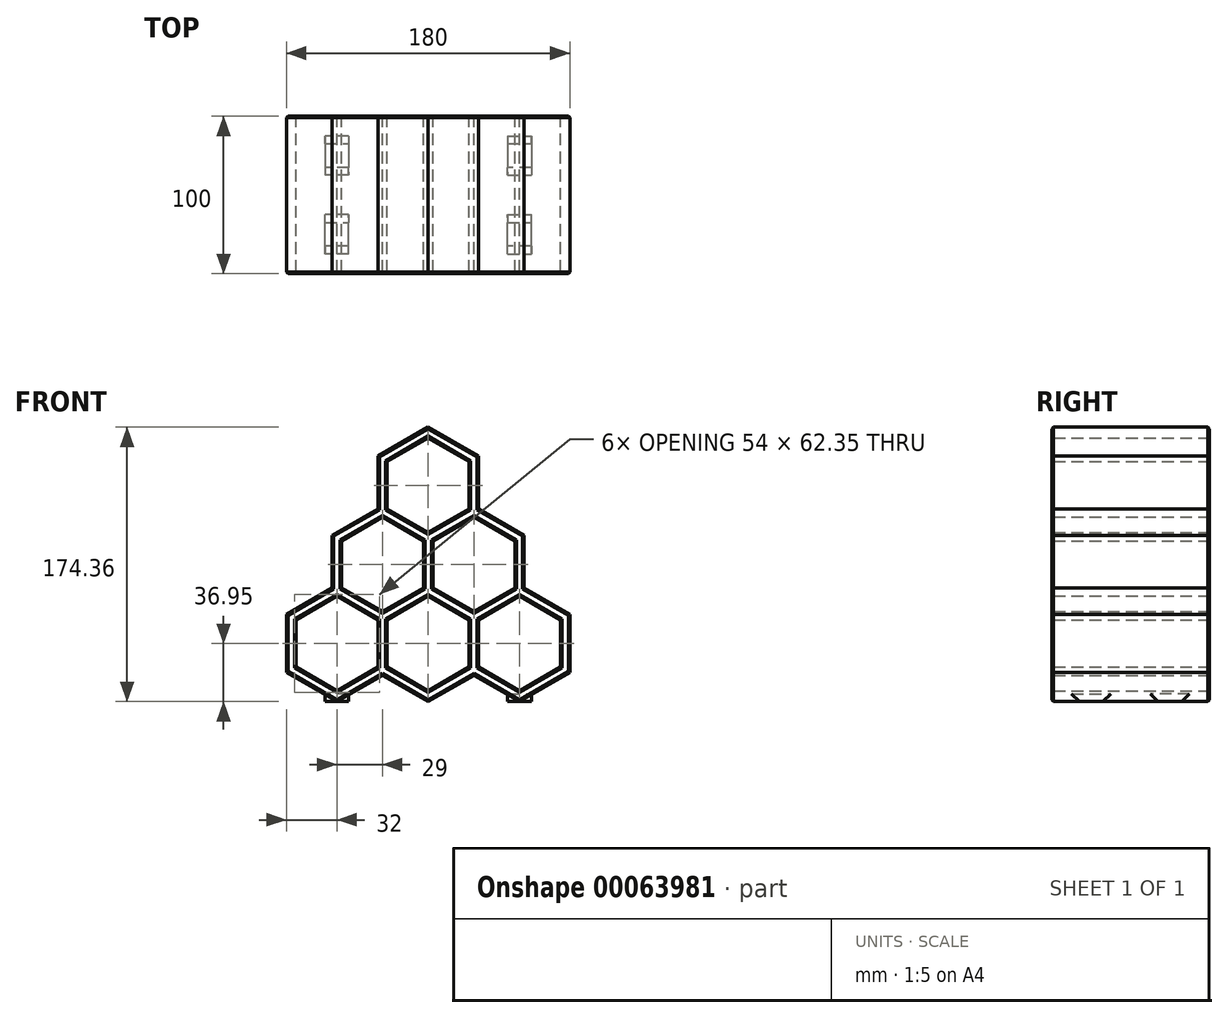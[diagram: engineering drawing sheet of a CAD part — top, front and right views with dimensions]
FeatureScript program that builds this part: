
annotation { "Feature Type Name" : "Feature", "Feature Type Description" : "" }
export const myFeature = defineFeature(function(context is Context, id is Id, definition is map)
    precondition{}
    {
        {
            var Q0;
            Q0=qCreatedBy(makeId("Front.planeOp"),FACE);
            var sketch = newSketch(context, id + "F0", { "sketchPlane" : qUnion([Q0])});
            skCircle(sketch, "E0.cCircle", {"center": v(0, 0) * mm, "radius": 32 * mm, "construction": true});
            skLineSegment(sketch, "E0.0", {"start": v(32, 18.48) * mm, "end": v(32, -18.48) * mm});
            skLineSegment(sketch, "E0.1", {"start": v(32, -18.48) * mm, "end": v(0, -36.95) * mm});
            skLineSegment(sketch, "E0.2", {"start": v(0, -36.95) * mm, "end": v(-32, -18.48) * mm});
            skLineSegment(sketch, "E0.3", {"start": v(-32, -18.48) * mm, "end": v(-32, 18.48) * mm});
            skLineSegment(sketch, "E0.4", {"start": v(-32, 18.48) * mm, "end": v(0, 36.95) * mm});
            skLineSegment(sketch, "E0.5", {"start": v(0, 36.95) * mm, "end": v(32, 18.48) * mm});
            skPoint(sketch, "E0.0.midPoint", {"position": v(32, 0) * mm});
            skCircle(sketch, "E1.cCircle", {"center": v(0, 0) * mm, "radius": 26 * mm, "construction": true});
            skLineSegment(sketch, "E1.0", {"start": v(26, 15.01) * mm, "end": v(26, -15.01) * mm});
            skLineSegment(sketch, "E1.1", {"start": v(26, -15.01) * mm, "end": v(0, -30.02) * mm});
            skLineSegment(sketch, "E1.2", {"start": v(0, -30.02) * mm, "end": v(-26, -15.01) * mm});
            skLineSegment(sketch, "E1.3", {"start": v(-26, -15.01) * mm, "end": v(-26, 15.01) * mm});
            skLineSegment(sketch, "E1.4", {"start": v(-26, 15.01) * mm, "end": v(0, 30.02) * mm});
            skLineSegment(sketch, "E1.5", {"start": v(0, 30.02) * mm, "end": v(26, 15.01) * mm});
            skPoint(sketch, "E1.0.midPoint", {"position": v(26, 0) * mm});
            skSolve(sketch);
        }
        {
            var Q0;
            Q0 = qSketchRegion(id + "F0", true);
            extrude(context, id + "F1", {"entities" : qUnion([Q0]), "depth" : 100 * mm});
        }
        {
            var Q0;
            Q0=makeQuery(id+"F1.opExtrude","CAP_EDGE",EDGE,{"disambiguationData":[OSD([sQuery(id+"F0.wireOp",EDGE,"E1.3")])],"isStart":false});
            cPoint(context, id + "F2", {"entities" : qUnion([Q0]), "parameter" : 0.5});
        }
        {
            var Q0;
            Q0=makeQuery(id+"F1.opExtrude","CAP_EDGE",EDGE,{"disambiguationData":[OSD([sQuery(id+"F0.wireOp",EDGE,"E0.0")])],"isStart":false});
            cPoint(context, id + "F3", {"entities" : qUnion([Q0]), "parameter" : 0.5});
        }
        {
            var Q0;
            Q0=makeQuery(id+"F1.opExtrude","SWEPT_BODY",BODY,{"disambiguationData":[OSD([sQuery(id+"F0.wireOp",EDGE,"E0.0"),sQuery(id+"F0.wireOp",EDGE,"E0.1"),sQuery(id+"F0.wireOp",EDGE,"E0.2"),sQuery(id+"F0.wireOp",EDGE,"E0.3"),sQuery(id+"F0.wireOp",EDGE,"E0.4"),sQuery(id+"F0.wireOp",EDGE,"E0.5"),sQuery(id+"F0.wireOp",EDGE,"E1.0"),sQuery(id+"F0.wireOp",EDGE,"E1.1"),sQuery(id+"F0.wireOp",EDGE,"E1.2"),sQuery(id+"F0.wireOp",EDGE,"E1.3"),sQuery(id+"F0.wireOp",EDGE,"E1.4"),sQuery(id+"F0.wireOp",EDGE,"E1.5")])]});
            var Q1;
            Q1 = qCreatedBy(id + "F2" ,VERTEX);
            var Q2;
            Q2 = qCreatedBy(id + "F3" ,VERTEX);
            transform(context, id + "F4", {"entities" : qUnion([Q0]), "transformType" : TransformType.TRANSLATION_ENTITY, "oppositeDirectionEntity" : false, "transformLine" : qUnion([Q1, Q2]), "makeCopy" : true});
        }
        {
            var Q0;
            Q0=makeQuery(id+"F1.opExtrude","CAP_EDGE",EDGE,{"disambiguationData":[OSD([sQuery(id+"F0.wireOp",EDGE,"E1.3")])],"isStart":false});
            cPoint(context, id + "F5", {"entities" : qUnion([Q0]), "parameter" : 0.5});
        }
        {
            var Q0;
            Q0=makeQuery(id+"F4.opPattern","COPY",EDGE,{"derivedFrom":makeQuery(id+"F1.opExtrude","CAP_EDGE",EDGE,{"disambiguationData":[OSD([sQuery(id+"F0.wireOp",EDGE,"E0.0")])],"isStart":false}),"instanceName":"1"});
            cPoint(context, id + "F6", {"entities" : qUnion([Q0]), "parameter" : 0.5});
        }
        {
            var Q0;
            Q0=makeQuery(id+"F1.opExtrude","SWEPT_BODY",BODY,{"disambiguationData":[OSD([sQuery(id+"F0.wireOp",EDGE,"E0.0"),sQuery(id+"F0.wireOp",EDGE,"E0.1"),sQuery(id+"F0.wireOp",EDGE,"E0.2"),sQuery(id+"F0.wireOp",EDGE,"E0.3"),sQuery(id+"F0.wireOp",EDGE,"E0.4"),sQuery(id+"F0.wireOp",EDGE,"E0.5"),sQuery(id+"F0.wireOp",EDGE,"E1.0"),sQuery(id+"F0.wireOp",EDGE,"E1.1"),sQuery(id+"F0.wireOp",EDGE,"E1.2"),sQuery(id+"F0.wireOp",EDGE,"E1.3"),sQuery(id+"F0.wireOp",EDGE,"E1.4"),sQuery(id+"F0.wireOp",EDGE,"E1.5")])]});
            var Q1;
            Q1 = qCreatedBy(id + "F5" ,VERTEX);
            var Q2;
            Q2 = qCreatedBy(id + "F6" ,VERTEX);
            transform(context, id + "F7", {"entities" : qUnion([Q0]), "transformType" : TransformType.TRANSLATION_ENTITY, "oppositeDirectionEntity" : false, "transformLine" : qUnion([Q1, Q2]), "makeCopy" : true});
        }
        {
            var Q0;
            Q0=makeQuery(id+"F1.opExtrude","CAP_EDGE",EDGE,{"disambiguationData":[OSD([sQuery(id+"F0.wireOp",EDGE,"E0.2")])],"isStart":false});
            cPoint(context, id + "F8", {"entities" : qUnion([Q0]), "parameter" : 0.5});
        }
        {
            var Q0;
            Q0=makeQuery(id+"F1.opExtrude","CAP_EDGE",EDGE,{"disambiguationData":[OSD([sQuery(id+"F0.wireOp",EDGE,"E1.5")])],"isStart":false});
            cPoint(context, id + "F9", {"entities" : qUnion([Q0]), "parameter" : 0.5});
        }
        {
            var Q0;
            Q0=makeQuery(id+"F1.opExtrude","SWEPT_BODY",BODY,{"disambiguationData":[OSD([sQuery(id+"F0.wireOp",EDGE,"E0.0"),sQuery(id+"F0.wireOp",EDGE,"E0.1"),sQuery(id+"F0.wireOp",EDGE,"E0.2"),sQuery(id+"F0.wireOp",EDGE,"E0.3"),sQuery(id+"F0.wireOp",EDGE,"E0.4"),sQuery(id+"F0.wireOp",EDGE,"E0.5"),sQuery(id+"F0.wireOp",EDGE,"E1.0"),sQuery(id+"F0.wireOp",EDGE,"E1.1"),sQuery(id+"F0.wireOp",EDGE,"E1.2"),sQuery(id+"F0.wireOp",EDGE,"E1.3"),sQuery(id+"F0.wireOp",EDGE,"E1.4"),sQuery(id+"F0.wireOp",EDGE,"E1.5")])]});
            var Q1;
            Q1 = qCreatedBy(id + "F8" ,VERTEX);
            var Q2;
            Q2 = qCreatedBy(id + "F9" ,VERTEX);
            transform(context, id + "F10", {"entities" : qUnion([Q0]), "transformType" : TransformType.TRANSLATION_ENTITY, "oppositeDirectionEntity" : false, "transformLine" : qUnion([Q1, Q2]), "makeCopy" : true});
        }
        {
            var Q0;
            Q0=makeQuery(id+"F1.opExtrude","CAP_EDGE",EDGE,{"disambiguationData":[OSD([sQuery(id+"F0.wireOp",EDGE,"E0.2")])],"isStart":false});
            cPoint(context, id + "F11", {"entities" : qUnion([Q0]), "parameter" : 0.5});
        }
        {
            var Q0;
            Q0=makeQuery(id+"F4.opPattern","COPY",EDGE,{"derivedFrom":makeQuery(id+"F1.opExtrude","CAP_EDGE",EDGE,{"disambiguationData":[OSD([sQuery(id+"F0.wireOp",EDGE,"E1.5")])],"isStart":false}),"instanceName":"1"});
            cPoint(context, id + "F12", {"entities" : qUnion([Q0]), "parameter" : 0.5});
        }
        {
            var Q0;
            Q0=makeQuery(id+"F1.opExtrude","SWEPT_BODY",BODY,{"disambiguationData":[OSD([sQuery(id+"F0.wireOp",EDGE,"E0.0"),sQuery(id+"F0.wireOp",EDGE,"E0.1"),sQuery(id+"F0.wireOp",EDGE,"E0.2"),sQuery(id+"F0.wireOp",EDGE,"E0.3"),sQuery(id+"F0.wireOp",EDGE,"E0.4"),sQuery(id+"F0.wireOp",EDGE,"E0.5"),sQuery(id+"F0.wireOp",EDGE,"E1.0"),sQuery(id+"F0.wireOp",EDGE,"E1.1"),sQuery(id+"F0.wireOp",EDGE,"E1.2"),sQuery(id+"F0.wireOp",EDGE,"E1.3"),sQuery(id+"F0.wireOp",EDGE,"E1.4"),sQuery(id+"F0.wireOp",EDGE,"E1.5")])]});
            var Q1;
            Q1 = qCreatedBy(id + "F11" ,VERTEX);
            var Q2;
            Q2 = qCreatedBy(id + "F12" ,VERTEX);
            transform(context, id + "F13", {"entities" : qUnion([Q0]), "transformType" : TransformType.TRANSLATION_ENTITY, "oppositeDirectionEntity" : false, "transformLine" : qUnion([Q1, Q2]), "makeCopy" : true});
        }
        {
            var Q0;
            Q0=makeQuery(id+"F1.opExtrude","CAP_EDGE",EDGE,{"disambiguationData":[OSD([sQuery(id+"F0.wireOp",EDGE,"E0.2")])],"isStart":false});
            cPoint(context, id + "F14", {"entities" : qUnion([Q0]), "parameter" : 0.5});
        }
        {
            var Q0;
            Q0=makeQuery(id+"F10.opPattern","COPY",EDGE,{"derivedFrom":makeQuery(id+"F1.opExtrude","CAP_EDGE",EDGE,{"disambiguationData":[OSD([sQuery(id+"F0.wireOp",EDGE,"E1.5")])],"isStart":false}),"instanceName":"1"});
            cPoint(context, id + "F15", {"entities" : qUnion([Q0]), "parameter" : 0.5});
        }
        {
            var Q0;
            Q0=makeQuery(id+"F1.opExtrude","SWEPT_BODY",BODY,{"disambiguationData":[OSD([sQuery(id+"F0.wireOp",EDGE,"E0.0"),sQuery(id+"F0.wireOp",EDGE,"E0.1"),sQuery(id+"F0.wireOp",EDGE,"E0.2"),sQuery(id+"F0.wireOp",EDGE,"E0.3"),sQuery(id+"F0.wireOp",EDGE,"E0.4"),sQuery(id+"F0.wireOp",EDGE,"E0.5"),sQuery(id+"F0.wireOp",EDGE,"E1.0"),sQuery(id+"F0.wireOp",EDGE,"E1.1"),sQuery(id+"F0.wireOp",EDGE,"E1.2"),sQuery(id+"F0.wireOp",EDGE,"E1.3"),sQuery(id+"F0.wireOp",EDGE,"E1.4"),sQuery(id+"F0.wireOp",EDGE,"E1.5")])]});
            var Q1;
            Q1 = qCreatedBy(id + "F14" ,VERTEX);
            var Q2;
            Q2 = qCreatedBy(id + "F15" ,VERTEX);
            transform(context, id + "F16", {"entities" : qUnion([Q0]), "transformType" : TransformType.TRANSLATION_ENTITY, "oppositeDirectionEntity" : false, "transformLine" : qUnion([Q1, Q2]), "makeCopy" : true});
        }
        {
            var Q0;
            Q0=makeQuery(id+"F1.opExtrude","SWEPT_BODY",BODY,{"disambiguationData":[OSD([sQuery(id+"F0.wireOp",EDGE,"E0.0"),sQuery(id+"F0.wireOp",EDGE,"E0.1"),sQuery(id+"F0.wireOp",EDGE,"E0.2"),sQuery(id+"F0.wireOp",EDGE,"E0.3"),sQuery(id+"F0.wireOp",EDGE,"E0.4"),sQuery(id+"F0.wireOp",EDGE,"E0.5"),sQuery(id+"F0.wireOp",EDGE,"E1.0"),sQuery(id+"F0.wireOp",EDGE,"E1.1"),sQuery(id+"F0.wireOp",EDGE,"E1.2"),sQuery(id+"F0.wireOp",EDGE,"E1.3"),sQuery(id+"F0.wireOp",EDGE,"E1.4"),sQuery(id+"F0.wireOp",EDGE,"E1.5")])]});
            var Q1;
            Q1=makeQuery(id+"F10.opPattern","COPY",BODY,{"derivedFrom":makeQuery(id+"F1.opExtrude","SWEPT_BODY",BODY,{"disambiguationData":[OSD([sQuery(id+"F0.wireOp",EDGE,"E0.0"),sQuery(id+"F0.wireOp",EDGE,"E0.1"),sQuery(id+"F0.wireOp",EDGE,"E0.2"),sQuery(id+"F0.wireOp",EDGE,"E0.3"),sQuery(id+"F0.wireOp",EDGE,"E0.4"),sQuery(id+"F0.wireOp",EDGE,"E0.5"),sQuery(id+"F0.wireOp",EDGE,"E1.0"),sQuery(id+"F0.wireOp",EDGE,"E1.1"),sQuery(id+"F0.wireOp",EDGE,"E1.2"),sQuery(id+"F0.wireOp",EDGE,"E1.3"),sQuery(id+"F0.wireOp",EDGE,"E1.4"),sQuery(id+"F0.wireOp",EDGE,"E1.5")])]}),"instanceName":"1"});
            var Q2;
            Q2=makeQuery(id+"F16.opPattern","COPY",BODY,{"derivedFrom":makeQuery(id+"F1.opExtrude","SWEPT_BODY",BODY,{"disambiguationData":[OSD([sQuery(id+"F0.wireOp",EDGE,"E0.0"),sQuery(id+"F0.wireOp",EDGE,"E0.1"),sQuery(id+"F0.wireOp",EDGE,"E0.2"),sQuery(id+"F0.wireOp",EDGE,"E0.3"),sQuery(id+"F0.wireOp",EDGE,"E0.4"),sQuery(id+"F0.wireOp",EDGE,"E0.5"),sQuery(id+"F0.wireOp",EDGE,"E1.0"),sQuery(id+"F0.wireOp",EDGE,"E1.1"),sQuery(id+"F0.wireOp",EDGE,"E1.2"),sQuery(id+"F0.wireOp",EDGE,"E1.3"),sQuery(id+"F0.wireOp",EDGE,"E1.4"),sQuery(id+"F0.wireOp",EDGE,"E1.5")])]}),"instanceName":"1"});
            var Q3;
            Q3=makeQuery(id+"F4.opPattern","COPY",BODY,{"derivedFrom":makeQuery(id+"F1.opExtrude","SWEPT_BODY",BODY,{"disambiguationData":[OSD([sQuery(id+"F0.wireOp",EDGE,"E0.0"),sQuery(id+"F0.wireOp",EDGE,"E0.1"),sQuery(id+"F0.wireOp",EDGE,"E0.2"),sQuery(id+"F0.wireOp",EDGE,"E0.3"),sQuery(id+"F0.wireOp",EDGE,"E0.4"),sQuery(id+"F0.wireOp",EDGE,"E0.5"),sQuery(id+"F0.wireOp",EDGE,"E1.0"),sQuery(id+"F0.wireOp",EDGE,"E1.1"),sQuery(id+"F0.wireOp",EDGE,"E1.2"),sQuery(id+"F0.wireOp",EDGE,"E1.3"),sQuery(id+"F0.wireOp",EDGE,"E1.4"),sQuery(id+"F0.wireOp",EDGE,"E1.5")])]}),"instanceName":"1"});
            var Q4;
            Q4=makeQuery(id+"F13.opPattern","COPY",BODY,{"derivedFrom":makeQuery(id+"F1.opExtrude","SWEPT_BODY",BODY,{"disambiguationData":[OSD([sQuery(id+"F0.wireOp",EDGE,"E0.0"),sQuery(id+"F0.wireOp",EDGE,"E0.1"),sQuery(id+"F0.wireOp",EDGE,"E0.2"),sQuery(id+"F0.wireOp",EDGE,"E0.3"),sQuery(id+"F0.wireOp",EDGE,"E0.4"),sQuery(id+"F0.wireOp",EDGE,"E0.5"),sQuery(id+"F0.wireOp",EDGE,"E1.0"),sQuery(id+"F0.wireOp",EDGE,"E1.1"),sQuery(id+"F0.wireOp",EDGE,"E1.2"),sQuery(id+"F0.wireOp",EDGE,"E1.3"),sQuery(id+"F0.wireOp",EDGE,"E1.4"),sQuery(id+"F0.wireOp",EDGE,"E1.5")])]}),"instanceName":"1"});
            var Q5;
            Q5=makeQuery(id+"F7.opPattern","COPY",BODY,{"derivedFrom":makeQuery(id+"F1.opExtrude","SWEPT_BODY",BODY,{"disambiguationData":[OSD([sQuery(id+"F0.wireOp",EDGE,"E0.0"),sQuery(id+"F0.wireOp",EDGE,"E0.1"),sQuery(id+"F0.wireOp",EDGE,"E0.2"),sQuery(id+"F0.wireOp",EDGE,"E0.3"),sQuery(id+"F0.wireOp",EDGE,"E0.4"),sQuery(id+"F0.wireOp",EDGE,"E0.5"),sQuery(id+"F0.wireOp",EDGE,"E1.0"),sQuery(id+"F0.wireOp",EDGE,"E1.1"),sQuery(id+"F0.wireOp",EDGE,"E1.2"),sQuery(id+"F0.wireOp",EDGE,"E1.3"),sQuery(id+"F0.wireOp",EDGE,"E1.4"),sQuery(id+"F0.wireOp",EDGE,"E1.5")])]}),"instanceName":"1"});
            booleanBodies(context, id + "F17", {"operationType" : BooleanOperationType.UNION, "tools" : qUnion([Q0, Q1, Q2, Q3, Q4, Q5])});
        }
        {
            var Q0;
            Q0=makeQuery(id+"F4.opPattern","COPY",EDGE,{"derivedFrom":makeQuery(id+"F1.opExtrude","CAP_EDGE",EDGE,{"disambiguationData":[OSD([sQuery(id+"F0.wireOp",EDGE,"E1.0")])],"isStart":false}),"instanceName":"1"});
            cPoint(context, id + "F18", {"entities" : qUnion([Q0]), "parameter" : 0.5});
        }
        {
            var Q0;
            Q0=makeQuery(id+"F1.opExtrude","CAP_EDGE",EDGE,{"disambiguationData":[OSD([sQuery(id+"F0.wireOp",EDGE,"E1.0")])],"isStart":false});
            cPoint(context, id + "F19", {"entities" : qUnion([Q0]), "parameter" : 0.5});
        }
        {
            var Q0;
            Q0=makeQuery(id+"F1.opExtrude","SWEPT_BODY",BODY,{"disambiguationData":[OSD([sQuery(id+"F0.wireOp",EDGE,"E0.0"),sQuery(id+"F0.wireOp",EDGE,"E0.1"),sQuery(id+"F0.wireOp",EDGE,"E0.2"),sQuery(id+"F0.wireOp",EDGE,"E0.3"),sQuery(id+"F0.wireOp",EDGE,"E0.4"),sQuery(id+"F0.wireOp",EDGE,"E0.5"),sQuery(id+"F0.wireOp",EDGE,"E1.0"),sQuery(id+"F0.wireOp",EDGE,"E1.1"),sQuery(id+"F0.wireOp",EDGE,"E1.2"),sQuery(id+"F0.wireOp",EDGE,"E1.3"),sQuery(id+"F0.wireOp",EDGE,"E1.4"),sQuery(id+"F0.wireOp",EDGE,"E1.5")])]});
            var Q1;
            Q1 = qCreatedBy(id + "F18" ,VERTEX);
            var Q2;
            Q2 = qCreatedBy(id + "F19" ,VERTEX);
            transform(context, id + "F20", {"entities" : qUnion([Q0]), "transformType" : TransformType.TRANSLATION_ENTITY, "oppositeDirectionEntity" : false, "transformLine" : qUnion([Q1, Q2]), "makeCopy" : false});
        }
        {
            var Q0;
            Q0=makeQuery(id+"F1.opExtrude","SWEPT_BODY",BODY,{"disambiguationData":[OSD([sQuery(id+"F0.wireOp",EDGE,"E0.0"),sQuery(id+"F0.wireOp",EDGE,"E0.1"),sQuery(id+"F0.wireOp",EDGE,"E0.2"),sQuery(id+"F0.wireOp",EDGE,"E0.3"),sQuery(id+"F0.wireOp",EDGE,"E0.4"),sQuery(id+"F0.wireOp",EDGE,"E0.5"),sQuery(id+"F0.wireOp",EDGE,"E1.0"),sQuery(id+"F0.wireOp",EDGE,"E1.1"),sQuery(id+"F0.wireOp",EDGE,"E1.2"),sQuery(id+"F0.wireOp",EDGE,"E1.3"),sQuery(id+"F0.wireOp",EDGE,"E1.4"),sQuery(id+"F0.wireOp",EDGE,"E1.5")])]});
            var Q1;
            Q1=makeQuery(id+"F4.opPattern","COPY",VERTEX,{"derivedFrom":makeQuery(id+"F1.opExtrude","CAP_VERTEX",VERTEX,{"disambiguationData":[OSD([sQuery(id+"F0.wireOp",EDGE,"E0.1"),sQuery(id+"F0.wireOp",EDGE,"E0.2")])],"isStart":true}),"instanceName":"1"});
            var Q2;
            Q2=qCreatedBy(makeId("Origin.pointOp"),VERTEX);
            transform(context, id + "F21", {"entities" : qUnion([Q0]), "transformType" : TransformType.TRANSLATION_ENTITY, "oppositeDirectionEntity" : false, "transformLine" : qUnion([Q1, Q2]), "makeCopy" : false});
        }
        {
            var Q0;
            Q0=qCreatedBy(makeId("Top.planeOp"),FACE);
            var sketch = newSketch(context, id + "F22", { "sketchPlane" : qUnion([Q0])});
            skLineSegment(sketch, "E2.0", {"start": v(-58, -100) * mm, "end": v(-58, 0) * mm, "construction": true});
            skLineSegment(sketch, "E2.1", {"start": v(58, -100) * mm, "end": v(58, 0) * mm, "construction": true});
            skLineSegment(sketch, "E2.2", {"start": v(0, -100) * mm, "end": v(0, 0) * mm, "construction": true});
            skLineSegment(sketch, "E3.bottom", {"start": v(-50.5, -87.5) * mm, "end": v(-65.5, -87.5) * mm});
            skLineSegment(sketch, "E3.top", {"start": v(-50.5, -62.5) * mm, "end": v(-65.5, -62.5) * mm});
            skLineSegment(sketch, "E3.left", {"start": v(-50.5, -87.5) * mm, "end": v(-50.5, -62.5) * mm});
            skLineSegment(sketch, "E3.right", {"start": v(-65.5, -87.5) * mm, "end": v(-65.5, -62.5) * mm});
            skPoint(sketch, "E3.middle", {"position": v(-58, -75) * mm});
            skLineSegment(sketch, "E4", {"start": v(-58, -50) * mm, "end": v(58, -50) * mm, "construction": true});
            skLineSegment(sketch, "E5.MirrorCS", {"start": v(65.5, -87.5) * mm, "end": v(65.5, -62.5) * mm});
            skLineSegment(sketch, "E6.MirrorCS", {"start": v(50.5, -87.5) * mm, "end": v(65.5, -87.5) * mm});
            skLineSegment(sketch, "E7.MirrorCS", {"start": v(50.5, -87.5) * mm, "end": v(50.5, -62.5) * mm});
            skLineSegment(sketch, "E8.MirrorCS", {"start": v(50.5, -62.5) * mm, "end": v(65.5, -62.5) * mm});
            skLineSegment(sketch, "E9.MirrorCS", {"start": v(50.5, -37.5) * mm, "end": v(65.5, -37.5) * mm});
            skLineSegment(sketch, "E10.MirrorCS", {"start": v(65.5, -12.5) * mm, "end": v(65.5, -37.5) * mm});
            skLineSegment(sketch, "E11.MirrorCS", {"start": v(50.5, -12.5) * mm, "end": v(65.5, -12.5) * mm});
            skLineSegment(sketch, "E12.MirrorCS", {"start": v(50.5, -12.5) * mm, "end": v(50.5, -37.5) * mm});
            skLineSegment(sketch, "E13.MirrorCS", {"start": v(-65.5, -12.5) * mm, "end": v(-65.5, -37.5) * mm});
            skLineSegment(sketch, "E14.MirrorCS", {"start": v(-50.5, -12.5) * mm, "end": v(-65.5, -12.5) * mm});
            skLineSegment(sketch, "E15.MirrorCS", {"start": v(-50.5, -12.5) * mm, "end": v(-50.5, -37.5) * mm});
            skLineSegment(sketch, "E16.MirrorCS", {"start": v(-50.5, -37.5) * mm, "end": v(-65.5, -37.5) * mm});
            skSolve(sketch);
        }
        {
            var Q0;
            Q0 = qSketchRegion(id + "F22", true);
            extrude(context, id + "F23", {"entities" : qUnion([Q0]), "depth" : 5 * mm});
        }
        {
            var Q0;
            Q0=makeQuery(id+"F23.opExtrude","CAP_EDGE",EDGE,{"disambiguationData":[OSD([sQuery(id+"F22.wireOp",EDGE,"E16.MirrorCS")])],"isStart":true});
            var Q1;
            Q1=makeQuery(id+"F23.opExtrude","CAP_EDGE",EDGE,{"disambiguationData":[OSD([sQuery(id+"F22.wireOp",EDGE,"E14.MirrorCS")])],"isStart":true});
            var Q2;
            Q2=makeQuery(id+"F23.opExtrude","CAP_EDGE",EDGE,{"disambiguationData":[OSD([sQuery(id+"F22.wireOp",EDGE,"E3.top")])],"isStart":true});
            var Q3;
            Q3=makeQuery(id+"F23.opExtrude","CAP_EDGE",EDGE,{"disambiguationData":[OSD([sQuery(id+"F22.wireOp",EDGE,"E3.bottom")])],"isStart":true});
            var Q4;
            Q4=makeQuery(id+"F23.opExtrude","CAP_EDGE",EDGE,{"disambiguationData":[OSD([sQuery(id+"F22.wireOp",EDGE,"E6.MirrorCS")])],"isStart":true});
            var Q5;
            Q5=makeQuery(id+"F23.opExtrude","CAP_EDGE",EDGE,{"disambiguationData":[OSD([sQuery(id+"F22.wireOp",EDGE,"E8.MirrorCS")])],"isStart":true});
            var Q6;
            Q6=makeQuery(id+"F23.opExtrude","CAP_EDGE",EDGE,{"disambiguationData":[OSD([sQuery(id+"F22.wireOp",EDGE,"E9.MirrorCS")])],"isStart":true});
            var Q7;
            Q7=makeQuery(id+"F23.opExtrude","CAP_EDGE",EDGE,{"disambiguationData":[OSD([sQuery(id+"F22.wireOp",EDGE,"E11.MirrorCS")])],"isStart":true});
            chamfer(context, id + "F24", {"entities" : qUnion([Q0, Q1, Q2, Q3, Q4, Q5, Q6, Q7]), "width" : 5 * mm, "tangentPropagation" : true});
        }
        {
            var Q0;
            {var subQ0=makeQuery(id+"F1.opExtrude","CAP_FACE",FACE,{"disambiguationData":[OSD([sQuery(id+"F0.wireOp",EDGE,"E0.0"),sQuery(id+"F0.wireOp",EDGE,"E0.1"),sQuery(id+"F0.wireOp",EDGE,"E0.2"),sQuery(id+"F0.wireOp",EDGE,"E0.3"),sQuery(id+"F0.wireOp",EDGE,"E0.4"),sQuery(id+"F0.wireOp",EDGE,"E0.5"),sQuery(id+"F0.wireOp",EDGE,"E1.0"),sQuery(id+"F0.wireOp",EDGE,"E1.1"),sQuery(id+"F0.wireOp",EDGE,"E1.2"),sQuery(id+"F0.wireOp",EDGE,"E1.3"),sQuery(id+"F0.wireOp",EDGE,"E1.4"),sQuery(id+"F0.wireOp",EDGE,"E1.5")])],"isStart":true});Q0=makeQuery(id+"F17.opBoolean","MERGE",FACE,{"derivedFrom":[subQ0,makeQuery(id+"F4.opPattern","COPY",FACE,{"derivedFrom":subQ0,"instanceName":"1"}),makeQuery(id+"F7.opPattern","COPY",FACE,{"derivedFrom":subQ0,"instanceName":"1"}),makeQuery(id+"F10.opPattern","COPY",FACE,{"derivedFrom":subQ0,"instanceName":"1"}),makeQuery(id+"F13.opPattern","COPY",FACE,{"derivedFrom":subQ0,"instanceName":"1"}),makeQuery(id+"F16.opPattern","COPY",FACE,{"derivedFrom":subQ0,"instanceName":"1"})]});}
            var Q1;
            {var subQ0=makeQuery(id+"F1.opExtrude","CAP_FACE",FACE,{"disambiguationData":[OSD([sQuery(id+"F0.wireOp",EDGE,"E0.0"),sQuery(id+"F0.wireOp",EDGE,"E0.1"),sQuery(id+"F0.wireOp",EDGE,"E0.2"),sQuery(id+"F0.wireOp",EDGE,"E0.3"),sQuery(id+"F0.wireOp",EDGE,"E0.4"),sQuery(id+"F0.wireOp",EDGE,"E0.5"),sQuery(id+"F0.wireOp",EDGE,"E1.0"),sQuery(id+"F0.wireOp",EDGE,"E1.1"),sQuery(id+"F0.wireOp",EDGE,"E1.2"),sQuery(id+"F0.wireOp",EDGE,"E1.3"),sQuery(id+"F0.wireOp",EDGE,"E1.4"),sQuery(id+"F0.wireOp",EDGE,"E1.5")])],"isStart":false});Q1=makeQuery(id+"F17.opBoolean","MERGE",FACE,{"derivedFrom":[subQ0,makeQuery(id+"F4.opPattern","COPY",FACE,{"derivedFrom":subQ0,"instanceName":"1"}),makeQuery(id+"F7.opPattern","COPY",FACE,{"derivedFrom":subQ0,"instanceName":"1"}),makeQuery(id+"F10.opPattern","COPY",FACE,{"derivedFrom":subQ0,"instanceName":"1"}),makeQuery(id+"F13.opPattern","COPY",FACE,{"derivedFrom":subQ0,"instanceName":"1"}),makeQuery(id+"F16.opPattern","COPY",FACE,{"derivedFrom":subQ0,"instanceName":"1"})]});}
            chamfer(context, id + "F25", {"entities" : qUnion([Q0, Q1]), "width" : 1 * mm, "tangentPropagation" : true});
        }
    });
